# Revit family: ВУТ_ВУЕ міні
name_source: partatom
category: Mechanical Equipment
units: mm (PartAtom-declared; Revit-internal decimal feet)

## family parameters
Always vertical = Yes
Classification = None
Cut with Voids When Loaded = No
Part Type = Normal
Room Calculation Point = No
Round Connector Dimension = Use Diameter
Shared = No
Work Plane-Based = No

## types (8) — shared parameters
00_20_Виробник = Вентс
00_20_Назва = Припливно-витяжна установка
B = 300 mm
D = 125 mm  [stored 0.410105 ft]
H = 443 mm  [stored 1.45341 ft]
L = 713 mm
Load Classification = HVAC
Manufacturer = Вентс
URL = https://vents.ua
b = 280 mm  [stored 0.918635 ft]
Діаметр = 125 mm  [stored 0.410105 ft]
Кількість фаз = 1
Матеріал зони обслуговуваня = <By Category>
Матеріал корпусу = Сталь, гальванизированная
Напруга = 230 V
Струм = 1 A
Частота = 50 Hz
Ширина = 300 mm
zero-valued in all types: Default Elevation

## per-type parameters (varying)
| type | H1 | L1 | Вент каналы вертикальные | Вент каналы горизонтальные | Висота | Довжина | Клас фільтрації | Клемная коробка сбоку | Клемная коробка сверху | Максимальний потік повітря | ПУ | Потужність | Рівень звукового тиску на відстані 3 м | Установлена потужність | Эл коробка большая сбоку | Эл коробка большая сверху |
| ВУЕ 250 В міні A1 | 490 mm  [stored 1.60761 ft] | 0 mm  [stored 0 ft] | Yes | No | 933 mm  [stored 3.06102 ft] | 0 mm  [stored 0 ft] | G4 | Yes | No | 260.0 m³/h | Yes | 126 W | 28...47 дБА | 138 VA | No | No |
| ВУЕ 250 Г міні A1 | 43 mm  [stored 0.141076 ft] | 810 mm | No | Yes | 486 mm  [stored 1.59449 ft] | 810 mm | G4 | No | Yes | 260.0 m³/h | No | 126 W | 28...47  дБА | 138 VA | No | No |
| ВУЕ 300 В2 міні ЕС A14 | 490 mm  [stored 1.60761 ft] | 0 mm  [stored 0 ft] | Yes | No | 933 mm  [stored 3.06102 ft] | 0 mm  [stored 0 ft] | G4, F8 | No | No | 300.0 m³/h | No | 165 W | 33 дБА | 299 VA | Yes | No |
| ВУЕ 300 Г2 міні ЕС A14 | 43 mm  [stored 0.141076 ft] | 810 mm | No | Yes | 486 mm  [stored 1.59449 ft] | 810 mm | G4, F8 | No | No | 300.0 m³/h | No | 165 W | 33  дБА | 299 VA | No | Yes |
| ВУТ 250 В міні A1 | 490 mm  [stored 1.60761 ft] | 0 mm  [stored 0 ft] | Yes | No | 933 mm  [stored 3.06102 ft] | 0 mm  [stored 0 ft] | G4 | Yes | No | 260.0 m³/h | Yes | 126 W | 28...47 дБА | 138 VA | No | No |
| ВУТ 250 Г міні A1 | 43 mm  [stored 0.141076 ft] | 810 mm | No | Yes | 486 mm  [stored 1.59449 ft] | 810 mm | G4 | No | Yes | 260.0 m³/h | No | 126 W | 28...47  дБА | 138 VA | No | No |
| ВУТ 300 В2 міні ЕС A14 | 490 mm  [stored 1.60761 ft] | 0 mm  [stored 0 ft] | Yes | No | 933 mm  [stored 3.06102 ft] | 0 mm  [stored 0 ft] | G4, F8 | No | No | 300.0 m³/h | No | 165 W | 33 дБА | 299 VA | Yes | No |
| ВУТ 300 Г2 міні ЕС A14 | 43 mm  [stored 0.141076 ft] | 810 mm | No | Yes | 486 mm  [stored 1.59449 ft] | 810 mm | G4, F8 | No | No | 300.0 m³/h | No | 165 W | 33  дБА | 299 VA | No | Yes |

note: column(s) folded — value = type name in every type: 00_20_Тип

note: [stored X ft] marks values corroborated as IEEE doubles in the binary element streams (Revit-internal decimal feet)
